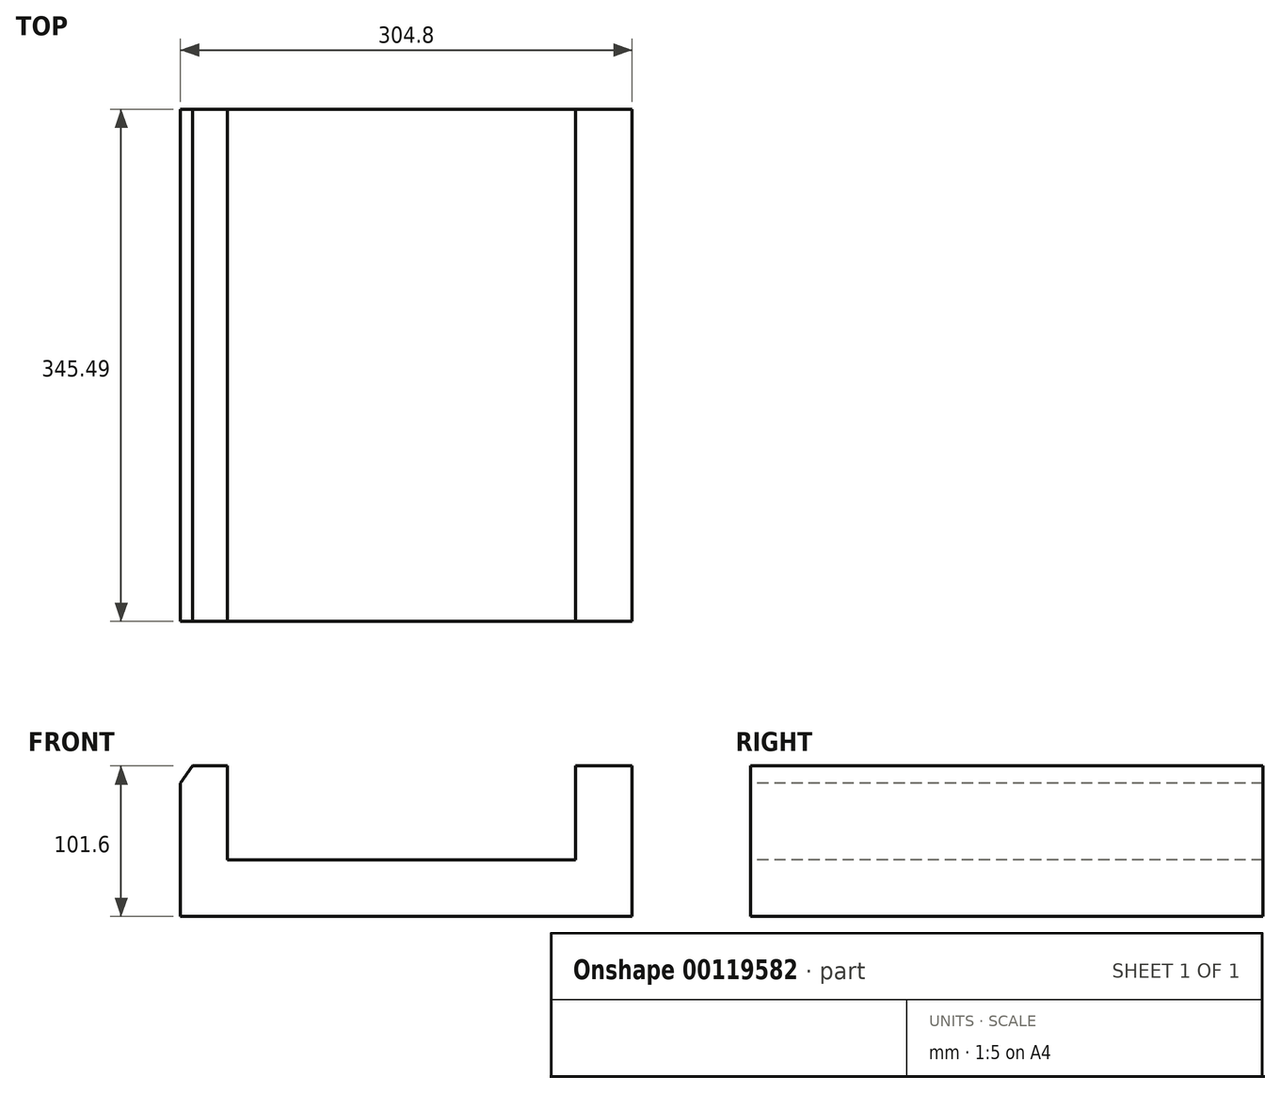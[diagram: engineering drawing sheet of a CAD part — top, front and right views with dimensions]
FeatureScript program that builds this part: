
annotation { "Feature Type Name" : "Feature", "Feature Type Description" : "" }
export const myFeature = defineFeature(function(context is Context, id is Id, definition is map)
    precondition{}
    {
        {
            var Q0;
            Q0=qCreatedBy(makeId("Top.planeOp"),FACE);
            var sketch = newSketch(context, id + "F0", { "sketchPlane" : qUnion([Q0])});
            skLineSegment(sketch, "E0.bottom", {"start": v(90.78, 0) * mm, "end": v(-214.02, 0) * mm});
            skLineSegment(sketch, "E0.top", {"start": v(90.78, 127) * mm, "end": v(-214.02, 127) * mm});
            skLineSegment(sketch, "E0.left", {"start": v(90.78, 0) * mm, "end": v(90.78, 127) * mm});
            skLineSegment(sketch, "E0.right", {"start": v(-214.02, 0) * mm, "end": v(-214.02, 127) * mm});
            skSolve(sketch);
        }
        {
            var Q0;
            Q0 = qSketchRegion(id + "F0", true);
            extrude(context, id + "F1", {"entities" : qUnion([Q0]), "oppositeDirection" : true, "depth" : 25.4 * mm});
        }
        {
            var Q0;
            Q0=makeQuery(id+"F1.opExtrude","SWEPT_FACE",FACE,{"disambiguationData":[OSD([sQuery(id+"F0.wireOp",EDGE,"E0.bottom")])]});
            var sketch = newSketch(context, id + "F2", { "sketchPlane" : qUnion([Q0])});
            skLineSegment(sketch, "E1", {"start": v(-214.02, -25.4) * mm, "end": v(-214.02, 64.4) * mm});
            skLineSegment(sketch, "E2", {"start": v(-214.02, 64.4) * mm, "end": v(-205.96, 76.2) * mm});
            skLineSegment(sketch, "E3", {"start": v(-205.96, 76.2) * mm, "end": v(-182.27, 76.2) * mm});
            skLineSegment(sketch, "E4", {"start": v(-182.27, 76.2) * mm, "end": v(-182.27, 12.7) * mm});
            skLineSegment(sketch, "E5", {"start": v(-182.27, 12.7) * mm, "end": v(52.68, 12.7) * mm});
            skLineSegment(sketch, "E6", {"start": v(52.68, 12.7) * mm, "end": v(52.68, 76.2) * mm});
            skLineSegment(sketch, "E7", {"start": v(52.68, 76.2) * mm, "end": v(90.78, 76.2) * mm});
            skLineSegment(sketch, "E8", {"start": v(90.78, 76.2) * mm, "end": v(90.78, -25.4) * mm});
            skLineSegment(sketch, "E9", {"start": v(90.78, -25.4) * mm, "end": v(-214.02, -25.4) * mm});
            skLineSegment(sketch, "E10", {"start": v(-182.27, 12.7) * mm, "end": v(-182.27, -25.4) * mm, "construction": true});
            skLineSegment(sketch, "E11", {"start": v(52.68, 23.65) * mm, "end": v(90.78, 23.65) * mm});
            skLineSegment(sketch, "E12", {"start": v(-182.27, 6) * mm, "end": v(90.78, 6) * mm, "construction": true});
            skLineSegment(sketch, "E13", {"start": v(90.78, 6) * mm, "end": v(90.53, 8.1) * mm, "construction": true});
            skLineSegment(sketch, "E14", {"start": v(-182.27, -6.35) * mm, "end": v(90.78, -6.35) * mm, "construction": true});
            skLineSegment(sketch, "E15", {"start": v(-182.27, -18.37) * mm, "end": v(90.78, -18.37) * mm, "construction": true});
            skLineSegment(sketch, "E16", {"start": v(90.78, -18.37) * mm, "end": v(91.37, -15.85) * mm, "construction": true});
            skLineSegment(sketch, "E17", {"start": v(52.68, 64) * mm, "end": v(90.78, 64) * mm, "construction": true});
            skLineSegment(sketch, "E18", {"start": v(52.68, 44.45) * mm, "end": v(90.78, 44.45) * mm, "construction": true});
            skLineSegment(sketch, "E19", {"start": v(52.68, 32.9) * mm, "end": v(90.78, 32.9) * mm, "construction": true});
            skSolve(sketch);
        }
        {
            var Q0;
            Q0 = qSketchRegion(id + "F2", true);
            extrude(context, id + "F3", {"entities" : qUnion([Q0]), "operationType" : NewBodyOperationType.ADD, "endBound" : BoundingType.THROUGH_ALL, "oppositeDirection" : true, "depth" : 25.4 * mm});
        }
    });
